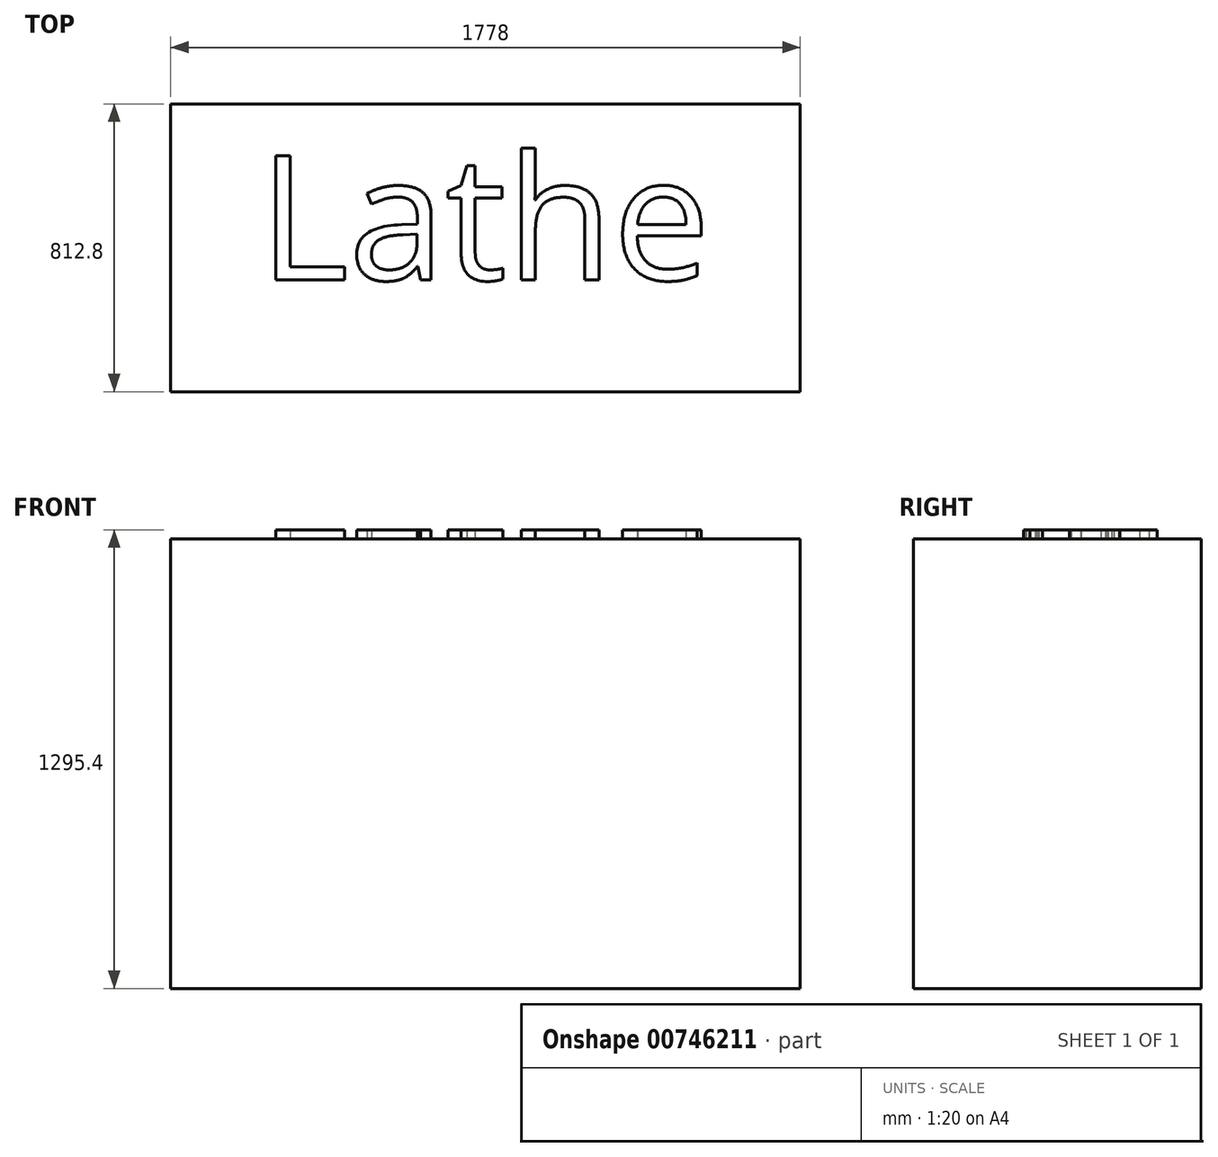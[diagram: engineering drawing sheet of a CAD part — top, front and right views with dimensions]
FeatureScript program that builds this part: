
annotation { "Feature Type Name" : "Feature", "Feature Type Description" : "" }
export const myFeature = defineFeature(function(context is Context, id is Id, definition is map)
    precondition{}
    {
        {
            var Q0;
            Q0=qCreatedBy(makeId("Top.planeOp"),FACE);
            var sketch = newSketch(context, id + "F0", { "sketchPlane" : qUnion([Q0])});
            skLineSegment(sketch, "E0.bottom", {"start": v(889, -406.4) * mm, "end": v(-889, -406.4) * mm});
            skLineSegment(sketch, "E0.top", {"start": v(889, 406.4) * mm, "end": v(-889, 406.4) * mm});
            skLineSegment(sketch, "E0.left", {"start": v(889, -406.4) * mm, "end": v(889, 406.4) * mm});
            skLineSegment(sketch, "E0.right", {"start": v(-889, -406.4) * mm, "end": v(-889, 406.4) * mm});
            skPoint(sketch, "E0.middle", {"position": v(0, 0) * mm});
            skSolve(sketch);
        }
        {
            var Q0;
            Q0 = qSketchRegion(id + "F0", true);
            extrude(context, id + "F1", {"entities" : qUnion([Q0]), "depth" : 1270 * mm, "offsetDistance" : 25.4 * mm});
        }
        {
            var Q0;
            Q0=makeQuery(id+"F1.opExtrude","CAP_FACE",FACE,{"disambiguationData":[OSD([sQuery(id+"F0.wireOp",EDGE,"E0.bottom"),sQuery(id+"F0.wireOp",EDGE,"E0.top"),sQuery(id+"F0.wireOp",EDGE,"E0.left"),sQuery(id+"F0.wireOp",EDGE,"E0.right")])],"isStart":false});
            var sketch = newSketch(context, id + "F2", { "sketchPlane" : qUnion([Q0])});
            skText(sketch, "E1", { "text": "Lathe", "fontName": "OpenSans-Regular.ttf"});
            const initialGuessF2  = {"E1": [-0.64071, -0.09063, 1, 0, 0.35276]};
            skSetInitialGuess(sketch, initialGuessF2);
            skSolve(sketch);
        }
        {
            var Q0;
            Q0 = qSketchRegion(id + "F2", true);
            extrude(context, id + "F3", {"entities" : qUnion([Q0]), "operationType" : NewBodyOperationType.ADD, "depth" : 25.4 * mm, "offsetDistance" : 25.4 * mm});
        }
    });
